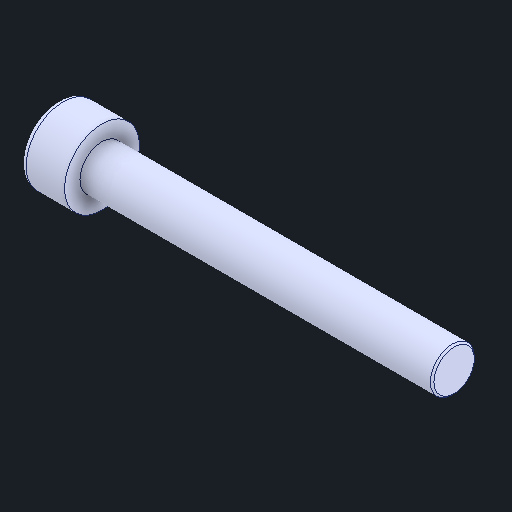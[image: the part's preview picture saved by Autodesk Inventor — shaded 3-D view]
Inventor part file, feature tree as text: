
AUTODESK INVENTOR PART (.ipt)
format: ipt  version: 2025 (Build 290162000, 162)  size: 111,616 bytes
history: native  units: mm
features: chamfer x1
ambient origin geometry x8: Origin, YZ Plane, XZ Plane, XY Plane, X Axis, Y Axis, Z Axis, Center Point
bodies: 实体1 (feature_tree)
feature tree (1):
  chamfer  "Chamfer1"  [1 undecoded]
note: 1 required parameter value undecoded (feature->parameter linkage not recoverable at this tier; creation-order binding heuristic only, values carry confidence <= 0.55)
